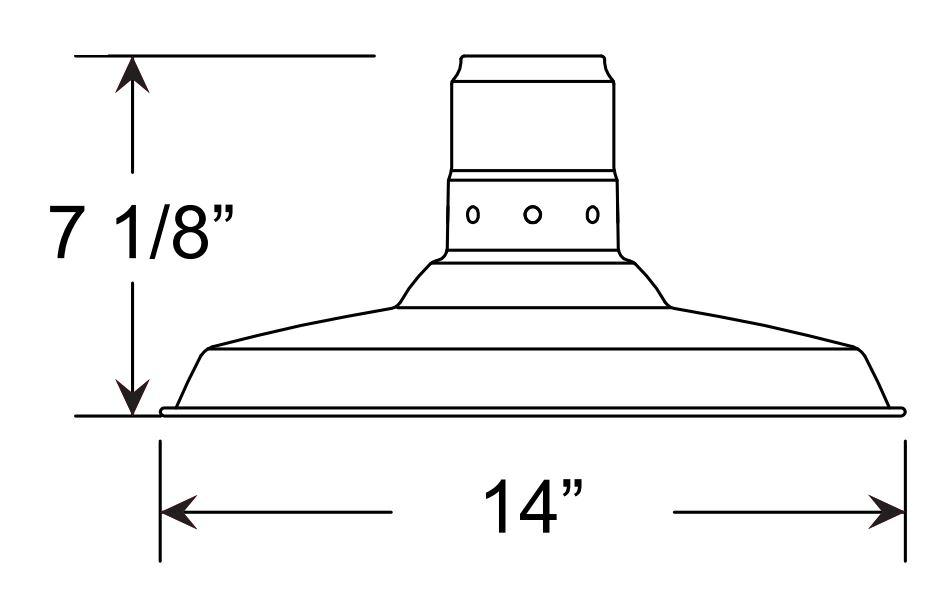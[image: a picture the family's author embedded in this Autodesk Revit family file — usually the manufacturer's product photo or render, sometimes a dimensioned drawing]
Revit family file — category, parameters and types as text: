
# Revit family: Sycamore 12,16,20,24 MB
name_source: partatom
category: Lighting Fixtures
units: mm (PartAtom-declared; Revit-internal decimal feet)

## family parameters
Always vertical = Yes
Cut with Voids When Loaded = No
Light Source = Yes
OmniClass Number = 23.80.70.00
OmniClass Title = Lighting
Part Type = Normal
Room Calculation Point = No
Round Connector Dimension = Use Diameter
Shared = No
Work Plane-Based = No

## types (4) — shared parameters
Apparent Load = 60 VA
Body Colour = Spun aluminium
Body Material = body
CRI = >90
Color Filter = 16777215
Construction Material = Heavy Duty spun aluminum.
Default Elevation = 0' - 0"
Description = 120-277 Voltage
Dimming = 1%
Dimming Lamp Color Temperature Shift = <None>
Efficiency = 65-125 lumens per watt
Fixture Finish = Fixture Finish
GLASS = Glass
Lamp = MB
Life = L70 50,000 hours
Load Classification = Lighting
Manufacturer = ANP Lighting
Power Factor = 1
Tilt Angle = 90.00°
URL = https://www.anplighting.com
Voltage = 277 V
Warranty = 5 year limited warranty
Wattage Comments = 60W Max

## per-type parameters (varying)
| type | Fixture Diameter | Fixture Height | MDS12 | MDS16 | MDS20 | MDS24 | Photometric Web File | Weight |
| MDS12 | 1' - 0" | 0' - 7 1/2" | Yes | No | No | No | MDS12M010LD35K.IES | 3.5 lbs |
| MDS16 | 1' - 4" | 0' - 10" | No | Yes | No | No | MDS12M010LD35K.IES | 4.0 lbs |
| MDS20 | 1' - 8" | 1' - 0 1/2" | No | No | Yes | No | MDS20M016LD35K.IES | 4.5 lbs |
| MDS24 | 1' - 8" | 1' - 3" | No | No | No | Yes | MDS20M016LD35K.IES | 5.0 lbs |

note: column(s) folded — value = type name in every type: Model

## geometry (parser evidence)
native form markers: Sweep x36
no freeform markers — native parametric forms only
